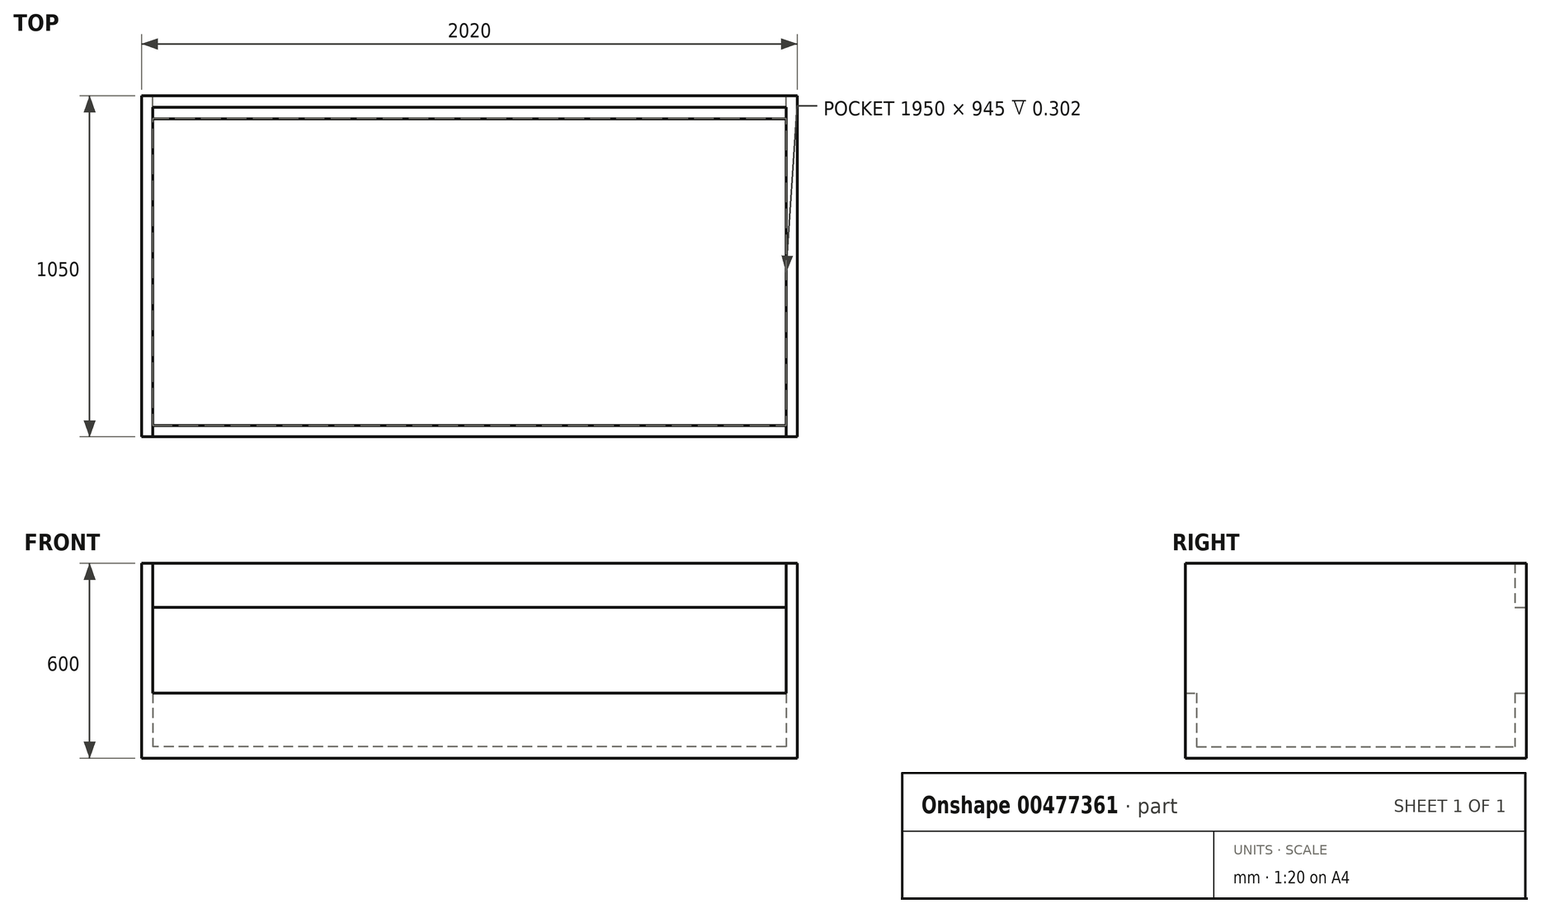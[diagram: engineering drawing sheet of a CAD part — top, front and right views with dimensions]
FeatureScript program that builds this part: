
annotation { "Feature Type Name" : "Feature", "Feature Type Description" : "" }
export const myFeature = defineFeature(function(context is Context, id is Id, definition is map)
    precondition{}
    {
        {
            var Q0;
            Q0=qCreatedBy(makeId("Front.planeOp"),FACE);
            var sketch = newSketch(context, id + "F0", { "sketchPlane" : qUnion([Q0])});
            skLineSegment(sketch, "E0.bottom", {"start": v(-975, 100) * mm, "end": v(975, 100) * mm});
            skLineSegment(sketch, "E0.top", {"start": v(-975, -100) * mm, "end": v(975, -100) * mm});
            skLineSegment(sketch, "E0.left", {"start": v(-975, 100) * mm, "end": v(-975, -100) * mm});
            skLineSegment(sketch, "E0.right", {"start": v(975, 100) * mm, "end": v(975, -100) * mm});
            skPoint(sketch, "E0.middle", {"position": v(0, 0) * mm});
            skLineSegment(sketch, "E1.bottom", {"start": v(-975, -100) * mm, "end": v(-1010, -100) * mm});
            skLineSegment(sketch, "E1.top", {"start": v(-975, 500) * mm, "end": v(-1010, 500) * mm});
            skLineSegment(sketch, "E1.left", {"start": v(-975, -100) * mm, "end": v(-975, 500) * mm});
            skLineSegment(sketch, "E1.right", {"start": v(-1010, -100) * mm, "end": v(-1010, 500) * mm});
            skLineSegment(sketch, "E2.bottom", {"start": v(975, -100) * mm, "end": v(1010, -100) * mm});
            skLineSegment(sketch, "E2.top", {"start": v(975, 500) * mm, "end": v(1010, 500) * mm});
            skLineSegment(sketch, "E2.left", {"start": v(975, -100) * mm, "end": v(975, 500) * mm});
            skLineSegment(sketch, "E2.right", {"start": v(1010, -100) * mm, "end": v(1010, 500) * mm});
            skLineSegment(sketch, "E3.bottom", {"start": v(-975, 500) * mm, "end": v(975, 500) * mm});
            skLineSegment(sketch, "E3.top", {"start": v(-975, 365) * mm, "end": v(975, 365) * mm});
            skLineSegment(sketch, "E3.left", {"start": v(-975, 500) * mm, "end": v(-975, 365) * mm});
            skLineSegment(sketch, "E3.right", {"start": v(975, 500) * mm, "end": v(975, 365) * mm});
            skLineSegment(sketch, "E4.top", {"start": v(-975, -65) * mm, "end": v(975, -65) * mm});
            skLineSegment(sketch, "E4.left", {"start": v(-975, -100) * mm, "end": v(-975, -65) * mm});
            skLineSegment(sketch, "E4.right", {"start": v(975, -100) * mm, "end": v(975, -65) * mm});
            skSolve(sketch);
        }
        {
            var Q0;
            Q0=makeQuery(id+"F0.imprint","IMPRINT",FACE,{"disambiguationData":[TD([[makeQuery(id+"F0.imprint","IMPRINT",EDGE,{"derivedFrom":sQuery(id+"F0.wireOp",EDGE,"E1.bottom")}),-1.0]])]});
            var Q1;
            Q1=makeQuery(id+"F0.imprint","IMPRINT",FACE,{"disambiguationData":[TD([[makeQuery(id+"F0.imprint","IMPRINT",EDGE,{"derivedFrom":sQuery(id+"F0.wireOp",EDGE,"E0.top")}),1.0]])]});
            var Q2;
            Q2=makeQuery(id+"F0.imprint","IMPRINT",FACE,{"disambiguationData":[TD([[makeQuery(id+"F0.imprint","IMPRINT",EDGE,{"derivedFrom":sQuery(id+"F0.wireOp",EDGE,"E2.bottom")}),1.0]])]});
            extrude(context, id + "F1", {"entities" : qUnion([Q0, Q1, Q2]), "depth" : 1050 * mm});
        }
        {
            var Q0;
            Q0 = qSketchRegion(id + "F0", true);
            var Q1;
            {var subQ0=sQuery(id+"F0.wireOp",EDGE,"E0.bottom");Q1=makeQuery(id+"F0.imprint","IMPRINT",FACE,{"disambiguationData":[TD([[makeQuery(id+"F0.imprint","IMPRINT",EDGE,{"derivedFrom":subQ0}),-1.0]])]});}
            extrude(context, id + "F2", {"entities" : qUnion([Q0, Q1]), "operationType" : NewBodyOperationType.ADD, "depth" : 35 * mm});
        }
        {
            var Q0;
            Q0=qCreatedBy(makeId("Right.planeOp"),FACE);
            var sketch = newSketch(context, id + "F3", { "sketchPlane" : qUnion([Q0])});
            skLineSegment(sketch, "E5.bottom", {"start": v(-1050, 100) * mm, "end": v(-1015, 100) * mm});
            skLineSegment(sketch, "E5.top", {"start": v(-1050, -100) * mm, "end": v(-1015, -100) * mm});
            skLineSegment(sketch, "E5.left", {"start": v(-1050, 100) * mm, "end": v(-1050, -100) * mm});
            skLineSegment(sketch, "E5.right", {"start": v(-1015, 100) * mm, "end": v(-1015, -100) * mm});
            skLineSegment(sketch, "E6.bottom", {"start": v(-1015, -100) * mm, "end": v(-980, -100) * mm});
            skLineSegment(sketch, "E6.top", {"start": v(-1015, -65) * mm, "end": v(-980, -65) * mm});
            skLineSegment(sketch, "E6.left", {"start": v(-1015, -100) * mm, "end": v(-1015, -65) * mm});
            skLineSegment(sketch, "E6.right", {"start": v(-980, -100) * mm, "end": v(-980, -65) * mm});
            skLineSegment(sketch, "E7.bottom", {"start": v(-70, -64.7) * mm, "end": v(-35, -64.7) * mm});
            skLineSegment(sketch, "E7.top", {"start": v(-70, -99.7) * mm, "end": v(-35, -99.7) * mm});
            skLineSegment(sketch, "E7.left", {"start": v(-70, -64.7) * mm, "end": v(-70, -99.7) * mm});
            skLineSegment(sketch, "E7.right", {"start": v(-35, -64.7) * mm, "end": v(-35, -99.7) * mm});
            skSolve(sketch);
        }
        {
            var Q0;
            Q0 = qSketchRegion(id + "F3", true);
            extrude(context, id + "F4", {"entities" : qUnion([Q0]), "operationType" : NewBodyOperationType.ADD, "endBound" : BoundingType.SYMMETRIC, "depth" : 1950 * mm});
        }
    });
